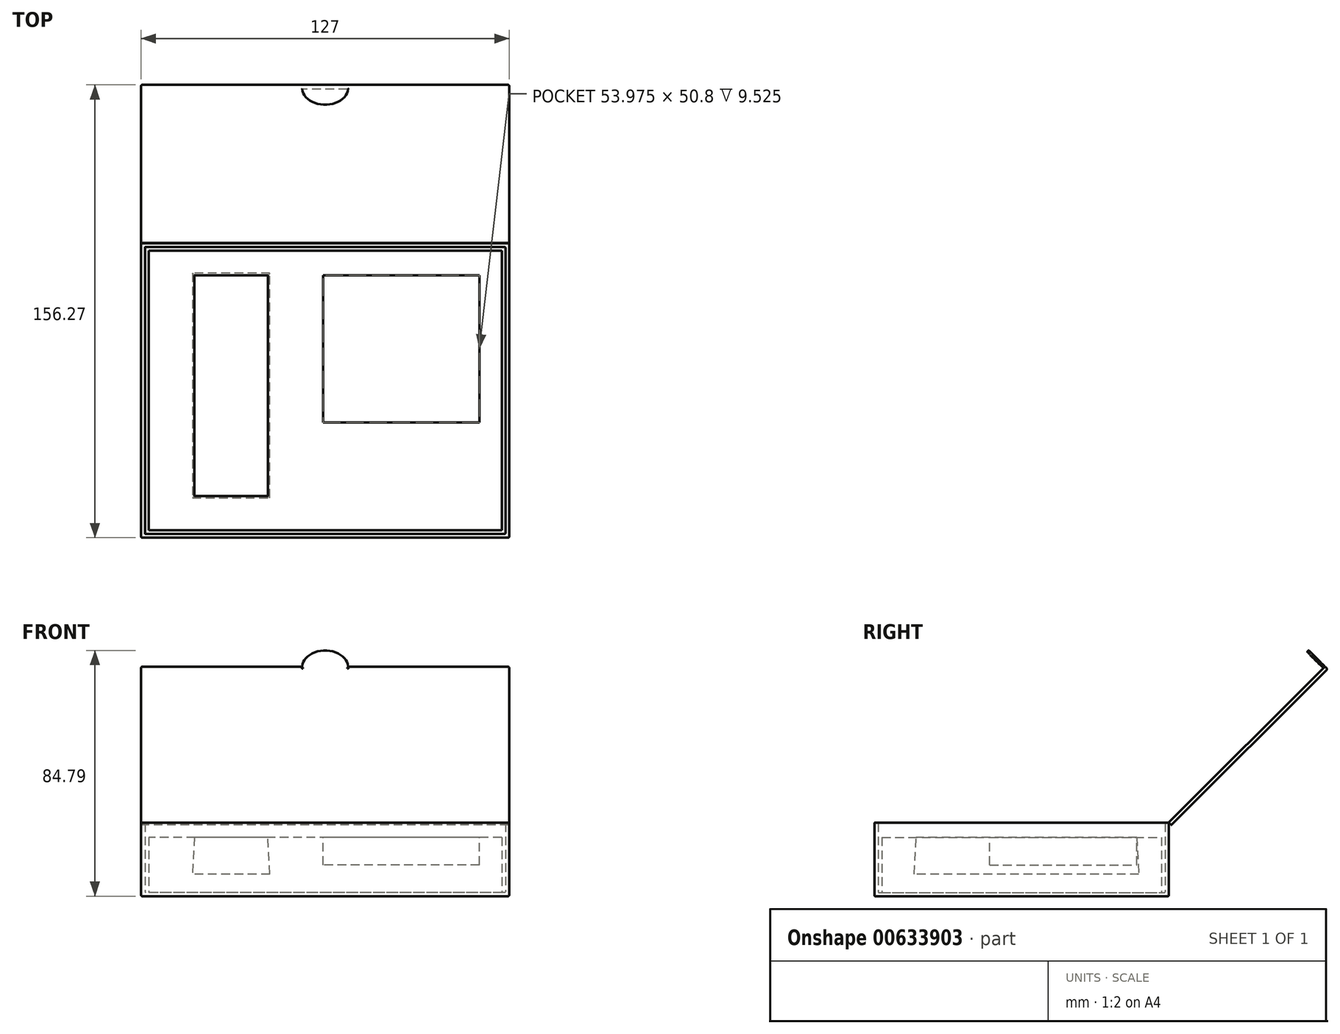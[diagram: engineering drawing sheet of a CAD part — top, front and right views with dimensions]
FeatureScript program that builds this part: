
annotation { "Feature Type Name" : "Feature", "Feature Type Description" : "" }
export const myFeature = defineFeature(function(context is Context, id is Id, definition is map)
    precondition{}
    {
        {
            var Q0;
            Q0=qCreatedBy(makeId("Top.planeOp"),FACE);
            var sketch = newSketch(context, id + "F0", { "sketchPlane" : qUnion([Q0])});
            skLineSegment(sketch, "E0.bottom", {"start": v(63.5, -50.8) * mm, "end": v(-63.5, -50.8) * mm});
            skLineSegment(sketch, "E0.top", {"start": v(63.5, 50.8) * mm, "end": v(-63.5, 50.8) * mm});
            skLineSegment(sketch, "E0.left", {"start": v(63.5, -50.8) * mm, "end": v(63.5, 50.8) * mm});
            skLineSegment(sketch, "E0.right", {"start": v(-63.5, -50.8) * mm, "end": v(-63.5, 50.8) * mm});
            skPoint(sketch, "E0.middle", {"position": v(0, 0) * mm});
            skSolve(sketch);
        }
        {
            var Q0;
            Q0=qSketchRegion(id+"F0",true);
            extrude(context, id + "F1", {"entities" : qUnion([Q0]), "depth" : 25.4 * mm, "offsetDistance" : 25.4 * mm});
        }
        {
            var Q0;
            Q0=makeQuery(id+"F1.opExtrude","CAP_FACE",FACE,{"disambiguationData":[OSD([sQuery(id+"F0.wireOp",EDGE,"E0.bottom"),sQuery(id+"F0.wireOp",EDGE,"E0.top"),sQuery(id+"F0.wireOp",EDGE,"E0.left"),sQuery(id+"F0.wireOp",EDGE,"E0.right")])],"isStart":false});
            shell(context, id + "F2", {"entities" : qUnion([Q0]), "thickness" : 1.27 * mm});
        }
        {
            var Q0;
            Q0=qCreatedBy(makeId("Right.planeOp"),FACE);
            var sketch = newSketch(context, id + "F3", { "sketchPlane" : qUnion([Q0])});
            skLineSegment(sketch, "E1.0.2", {"start": v(50.8, 25.4) * mm, "end": v(-50.8, 25.4) * mm, "construction": true});
            skLineSegment(sketch, "E2", {"start": v(50.8, 25.4) * mm, "end": v(104.68, 79.28) * mm});
            skLineSegment(sketch, "E3.0", {"start": v(51.7, 24.5) * mm, "end": v(105.58, 78.38) * mm});
            skLineSegment(sketch, "E4", {"start": v(50.8, 25.4) * mm, "end": v(51.7, 24.5) * mm});
            skLineSegment(sketch, "E5", {"start": v(104.68, 79.28) * mm, "end": v(105.58, 78.38) * mm});
            skSolve(sketch);
        }
        {
            var Q0;
            Q0=qSketchRegion(id+"F3",true);
            var Q1;
            Q1=makeQuery(id+"F1.opExtrude","SWEPT_FACE",FACE,{"disambiguationData":[OSD([sQuery(id+"F0.wireOp",EDGE,"E0.left")])]});
            var Q2;
            Q2=makeQuery(id+"F1.opExtrude","SWEPT_FACE",FACE,{"disambiguationData":[OSD([sQuery(id+"F0.wireOp",EDGE,"E0.right")])]});
            extrude(context, id + "F4", {"entities" : qUnion([Q0]), "endBound" : BoundingType.UP_TO_SURFACE, "depth" : 25.4 * mm, "endBoundEntityFace" : qUnion([Q1]), "offsetDistance" : 25.4 * mm, "hasSecondDirection" : true, "secondDirectionBound" : SecondDirectionBoundingType.UP_TO_SURFACE, "secondDirectionOppositeDirection" : true, "secondDirectionDepth" : 25.4 * mm, "secondDirectionBoundEntityFace" : qUnion([Q2])});
        }
        {
            var Q0;
            Q0=makeQuery(id+"F1.opExtrude","SWEPT_EDGE",EDGE,{"disambiguationData":[OSD([sQuery(id+"F0.wireOp",EDGE,"E0.bottom"),sQuery(id+"F0.wireOp",EDGE,"E0.left")])]});
            var Q1;
            Q1=makeQuery(id+"F1.opExtrude","SWEPT_EDGE",EDGE,{"disambiguationData":[OSD([sQuery(id+"F0.wireOp",EDGE,"E0.bottom"),sQuery(id+"F0.wireOp",EDGE,"E0.right")])]});
            var Q2;
            Q2=makeQuery(id+"F1.opExtrude","CAP_FACE",FACE,{"disambiguationData":[OSD([sQuery(id+"F0.wireOp",EDGE,"E0.bottom"),sQuery(id+"F0.wireOp",EDGE,"E0.top"),sQuery(id+"F0.wireOp",EDGE,"E0.left"),sQuery(id+"F0.wireOp",EDGE,"E0.right")])],"isStart":true});
            var Q3;
            Q3=makeQuery(id+"F2.opShell","OFFSET_FACE",FACE,{"disambiguationData":[OSD([sQuery(id+"F0.wireOp",EDGE,"E0.bottom"),sQuery(id+"F0.wireOp",EDGE,"E0.top"),sQuery(id+"F0.wireOp",EDGE,"E0.left"),sQuery(id+"F0.wireOp",EDGE,"E0.right")])]});
            var Q4;
            Q4=makeQuery(id+"F2.opShell","OFFSET_FACE",FACE,{"disambiguationData":[OSD([sQuery(id+"F0.wireOp",EDGE,"E0.bottom")])]});
            var Q5;
            Q5=makeQuery(id+"F2.opShell","OFFSET_FACE",FACE,{"disambiguationData":[OSD([sQuery(id+"F0.wireOp",EDGE,"E0.top")])]});
            var Q6;
            Q6=makeQuery(id+"F1.opExtrude","CAP_FACE",FACE,{"disambiguationData":[OSD([sQuery(id+"F0.wireOp",EDGE,"E0.bottom"),sQuery(id+"F0.wireOp",EDGE,"E0.top"),sQuery(id+"F0.wireOp",EDGE,"E0.left"),sQuery(id+"F0.wireOp",EDGE,"E0.right")])],"isStart":false});
            fillet(context, id + "F5", {"entities" : qUnion([Q0, Q1, Q2, Q3, Q4, Q5, Q6]), "radius" : 0.25 * mm, "tangentPropagation" : true, "allowEdgeOverflow" : false});
        }
        {
            var Q0;
            Q0=makeQuery(id+"F4.opExtrude","SWEPT_FACE",FACE,{"disambiguationData":[OSD([sQuery(id+"F3.wireOp",EDGE,"E5")])]});
            var sketch = newSketch(context, id + "F6", { "sketchPlane" : qUnion([Q0])});
            skArc(sketch, "E6", {"start": v(7.94, -17.96) * mm, "mid": v(0, -10.02) * mm, "end": v(-7.94, -17.96) * mm});
            skLineSegment(sketch, "E7", {"start": v(-7.94, -17.96) * mm, "end": v(7.94, -17.96) * mm});
            skSolve(sketch);
        }
        {
            var Q0;
            Q0=qSketchRegion(id+"F6",true);
            extrude(context, id + "F7", {"entities" : qUnion([Q0]), "operationType" : NewBodyOperationType.ADD, "oppositeDirection" : true, "depth" : 0.76 * mm, "offsetDistance" : 25.4 * mm});
        }
        {
            var Q0;
            Q0=makeQuery(id+"F4.opExtrude","SWEPT_FACE",FACE,{"disambiguationData":[OSD([sQuery(id+"F3.wireOp",EDGE,"E3.0")])]});
            var Q1;
            Q1=makeQuery(id+"F4.opExtrude","SWEPT_FACE",FACE,{"disambiguationData":[OSD([sQuery(id+"F3.wireOp",EDGE,"E2")])]});
            var Q2;
            Q2=makeQuery(id+"F4.opExtrude","SWEPT_FACE",FACE,{"disambiguationData":[OSD([sQuery(id+"F3.wireOp",EDGE,"E5")])]});
            var Q3;
            Q3=makeQuery(id+"F7.opExtrude","CAP_EDGE",EDGE,{"disambiguationData":[OSD([sQuery(id+"F6.wireOp",EDGE,"E6")])],"isStart":false});
            fillet(context, id + "F8", {"entities" : qUnion([Q0, Q1, Q2, Q3]), "radius" : 0.25 * mm, "tangentPropagation" : true, "allowEdgeOverflow" : false});
        }
        {
            var Q0;
            Q0=makeQuery(id+"F4.opExtrude","SWEPT_FACE",FACE,{"disambiguationData":[OSD([sQuery(id+"F3.wireOp",EDGE,"E2")])]});
            var sketch = newSketch(context, id + "F9", { "sketchPlane" : qUnion([Q0])});
            skPoint(sketch, "E8", {"position": v(-63.25, 91.98) * mm});
            skPoint(sketch, "E9", {"position": v(0, 130.08) * mm});
            skText(sketch, "E10", { "text": "Welcome to the Future.", "fontName": "OpenSans-Regular.ttf"});
            const initialGuessF9  = {"E10": [-0.0508, 0.08892, 1, 0, 0.00671]};
            skSetInitialGuess(sketch, initialGuessF9);
            skSolve(sketch);
        }
        {
            var Q0;
            Q0=makeQuery(id+"F2.opShell","OFFSET_FACE",FACE,{"disambiguationData":[OSD([sQuery(id+"F0.wireOp",EDGE,"E0.bottom"),sQuery(id+"F0.wireOp",EDGE,"E0.top"),sQuery(id+"F0.wireOp",EDGE,"E0.left"),sQuery(id+"F0.wireOp",EDGE,"E0.right")])]});
            var sketch = newSketch(context, id + "F10", { "sketchPlane" : qUnion([Q0])});
            skLineSegment(sketch, "E11.0", {"start": v(60.96, 48.26) * mm, "end": v(-60.96, 48.26) * mm});
            skLineSegment(sketch, "E11.1", {"start": v(60.96, -48.26) * mm, "end": v(60.96, 48.26) * mm});
            skLineSegment(sketch, "E11.2", {"start": v(60.96, -48.26) * mm, "end": v(-60.96, -48.26) * mm});
            skLineSegment(sketch, "E11.3", {"start": v(-60.96, -48.26) * mm, "end": v(-60.96, 48.26) * mm});
            skSolve(sketch);
        }
        {
            var Q0;
            Q0=qSketchRegion(id+"F10",true);
            extrude(context, id + "F11", {"entities" : qUnion([Q0]), "depth" : 19.05 * mm, "offsetDistance" : 25.4 * mm});
        }
        {
            var Q0;
            Q0=makeQuery(id+"F11.opExtrude","CAP_FACE",FACE,{"disambiguationData":[OSD([sQuery(id+"F10.wireOp",EDGE,"E11.0"),sQuery(id+"F10.wireOp",EDGE,"E11.1"),sQuery(id+"F10.wireOp",EDGE,"E11.2"),sQuery(id+"F10.wireOp",EDGE,"E11.3")])],"isStart":false});
            var sketch = newSketch(context, id + "F12", { "sketchPlane" : qUnion([Q0])});
            skLineSegment(sketch, "E12.bottom", {"start": v(53.28, -11.01) * mm, "end": v(-0.7, -11.01) * mm});
            skLineSegment(sketch, "E12.top", {"start": v(53.28, 39.79) * mm, "end": v(-0.7, 39.79) * mm});
            skLineSegment(sketch, "E12.left", {"start": v(53.28, -11.01) * mm, "end": v(53.28, 39.79) * mm});
            skLineSegment(sketch, "E12.right", {"start": v(-0.7, -11.01) * mm, "end": v(-0.7, 39.79) * mm});
            skPoint(sketch, "E12.middle", {"position": v(26.3, 14.39) * mm});
            skPoint(sketch, "E12.middle.positionSnap0", {"position": v(-60.96, 0) * mm});
            skPoint(sketch, "E12.middle.positionSnap1", {"position": v(0, 48.26) * mm});
            skPoint(sketch, "E12.centerSnap0", {"position": v(-60.96, 0) * mm});
            skPoint(sketch, "E12.centerSnap1", {"position": v(0, 48.26) * mm});
            skSolve(sketch);
        }
        {
            var Q0;
            Q0=qSketchRegion(id+"F12",true);
            extrude(context, id + "F13", {"entities" : qUnion([Q0]), "operationType" : NewBodyOperationType.REMOVE, "oppositeDirection" : true, "depth" : 9.52 * mm, "offsetDistance" : 25.4 * mm});
        }
        {
            var Q0;
            Q0=makeQuery(id+"F11.opExtrude","CAP_FACE",FACE,{"disambiguationData":[OSD([sQuery(id+"F10.wireOp",EDGE,"E11.0"),sQuery(id+"F10.wireOp",EDGE,"E11.1"),sQuery(id+"F10.wireOp",EDGE,"E11.2"),sQuery(id+"F10.wireOp",EDGE,"E11.3")])],"isStart":false});
            var sketch = newSketch(context, id + "F14", { "sketchPlane" : qUnion([Q0])});
            skLineSegment(sketch, "E13.bottom", {"start": v(-45.15, 39.79) * mm, "end": v(-19.75, 39.79) * mm});
            skLineSegment(sketch, "E13.top", {"start": v(-45.15, -36.41) * mm, "end": v(-19.75, -36.41) * mm});
            skLineSegment(sketch, "E13.left", {"start": v(-45.15, 39.79) * mm, "end": v(-45.15, -36.41) * mm});
            skLineSegment(sketch, "E13.right", {"start": v(-19.75, 39.79) * mm, "end": v(-19.75, -36.41) * mm});
            skSolve(sketch);
        }
        {
            var Q0;
            Q0 = qSketchRegion(id + "F14", true);
            extrude(context, id + "F15", {"entities" : qUnion([Q0]), "operationType" : NewBodyOperationType.REMOVE, "oppositeDirection" : true, "depth" : 12.7 * mm, "offsetDistance" : 25.4 * mm, "hasDraft" : true, "draftAngle" : 3 * degree});
        }
    });
